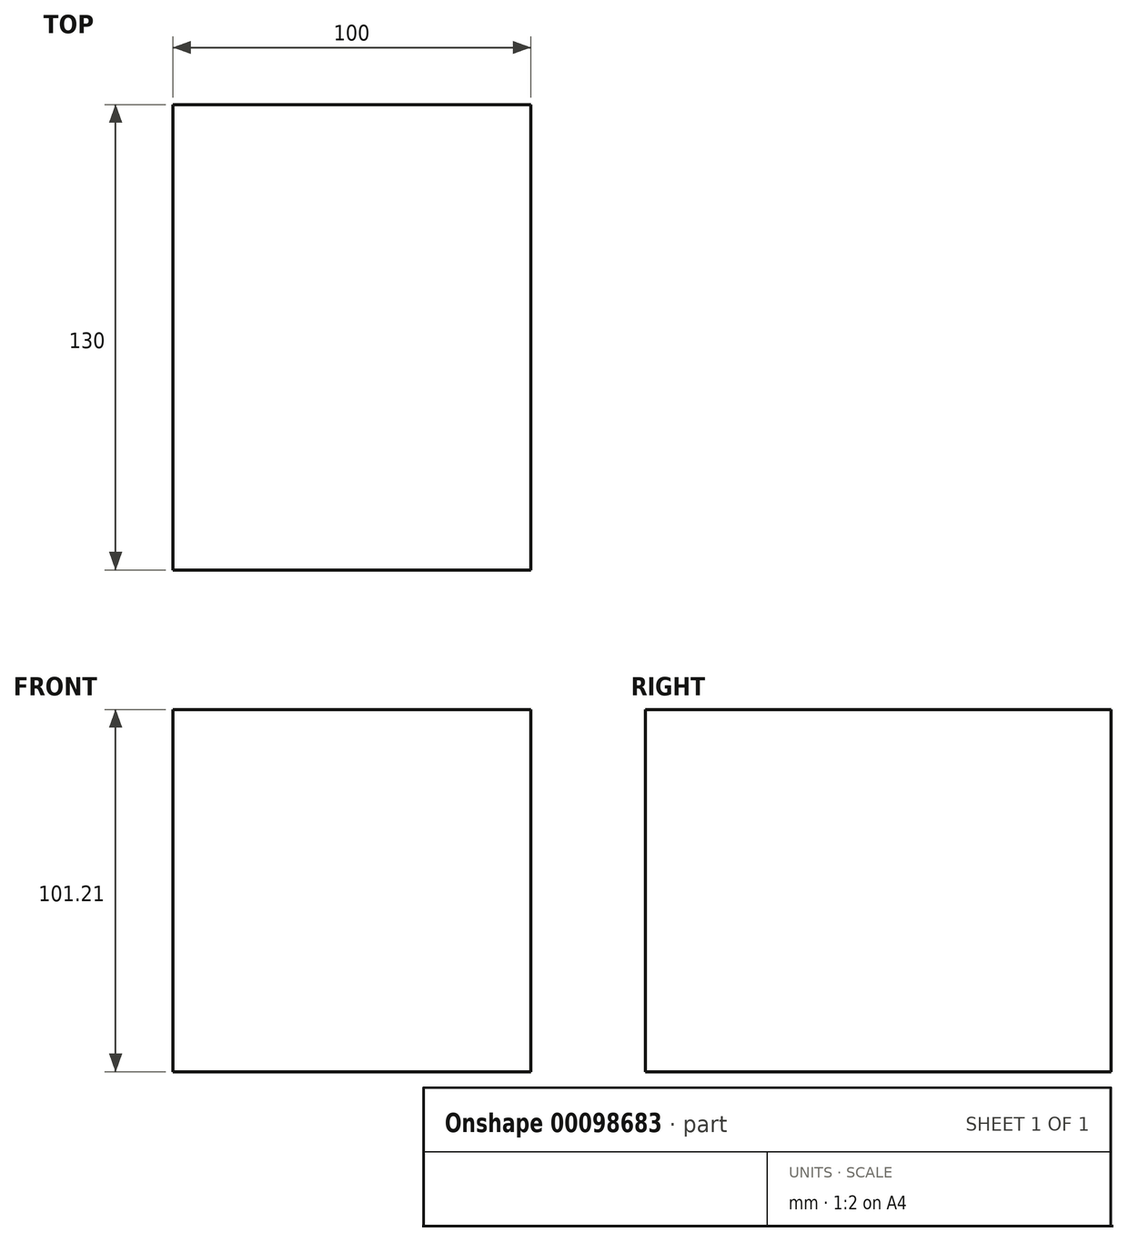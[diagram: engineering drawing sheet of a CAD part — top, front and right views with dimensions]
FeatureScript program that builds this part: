
annotation { "Feature Type Name" : "Feature", "Feature Type Description" : "" }
export const myFeature = defineFeature(function(context is Context, id is Id, definition is map)
    precondition{}
    {
        {
            var Q0;
            Q0=qCreatedBy(makeId("Top.planeOp"),FACE);
            var sketch = newSketch(context, id + "F0", { "sketchPlane" : qUnion([Q0])});
            skLineSegment(sketch, "E0.bottom", {"start": v(-45.8, -46.07) * mm, "end": v(54.2, -46.07) * mm});
            skLineSegment(sketch, "E0.top", {"start": v(-45.8, 83.93) * mm, "end": v(54.2, 83.93) * mm});
            skLineSegment(sketch, "E0.left", {"start": v(-45.8, -46.07) * mm, "end": v(-45.8, 83.93) * mm});
            skLineSegment(sketch, "E0.right", {"start": v(54.2, -46.07) * mm, "end": v(54.2, 83.93) * mm});
            skSolve(sketch);
        }
        {
            var Q0;
            Q0=makeQuery(id+"F0.imprint","IMPRINT",FACE,{"disambiguationData":[TD([[makeQuery(id+"F0.imprint","IMPRINT",EDGE,{"derivedFrom":sQuery(id+"F0.wireOp",EDGE,"E0.bottom")}),1.0]])]});
            extrude(context, id + "F1", {"entities" : qUnion([Q0]), "depth" : 101.2 * mm});
        }
    });
